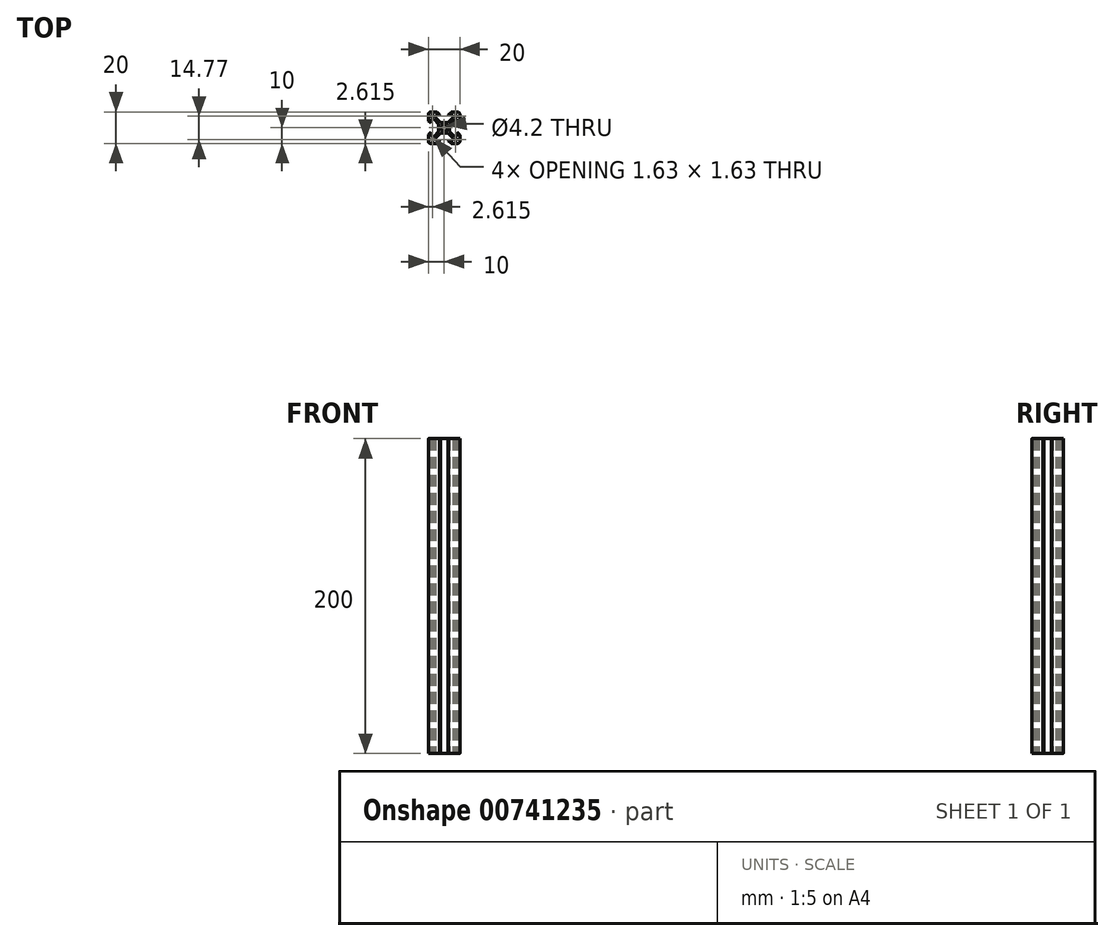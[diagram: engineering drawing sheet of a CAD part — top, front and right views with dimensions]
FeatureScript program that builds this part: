
annotation { "Feature Type Name" : "Feature", "Feature Type Description" : "" }
export const myFeature = defineFeature(function(context is Context, id is Id, definition is map)
    precondition{}
    {
        {
            var Q0;
            Q0=qCreatedBy(makeId("Top.planeOp"),FACE);
            var sketch = newSketch(context, id + "F0", { "sketchPlane" : qUnion([Q0])});
            skLineSegment(sketch, "E0", {"start": v(-8.2, -8.2) * mm, "end": v(-6.57, -8.2) * mm});
            skLineSegment(sketch, "E1", {"start": v(-8.2, -6.57) * mm, "end": v(-8.2, -8.2) * mm});
            skLineSegment(sketch, "E2", {"start": v(-7.66, -6.57) * mm, "end": v(-8.2, -6.57) * mm});
            skLineSegment(sketch, "E3", {"start": v(-6.57, -7.66) * mm, "end": v(-7.66, -6.57) * mm});
            skLineSegment(sketch, "E4", {"start": v(-6.57, -8.2) * mm, "end": v(-6.57, -7.66) * mm});
            skLineSegment(sketch, "E5", {"start": v(7.66, -6.57) * mm, "end": v(6.57, -7.66) * mm});
            skLineSegment(sketch, "E6", {"start": v(8.2, -6.57) * mm, "end": v(7.66, -6.57) * mm});
            skLineSegment(sketch, "E7", {"start": v(8.2, -8.2) * mm, "end": v(8.2, -6.57) * mm});
            skLineSegment(sketch, "E8", {"start": v(6.57, -8.2) * mm, "end": v(8.2, -8.2) * mm});
            skLineSegment(sketch, "E9", {"start": v(6.57, -7.66) * mm, "end": v(6.57, -8.2) * mm});
            skCircle(sketch, "E10", {"center": v(0, 0) * mm, "radius": 2.1 * mm});
            skLineSegment(sketch, "E11", {"start": v(8.2, 8.2) * mm, "end": v(6.57, 8.2) * mm});
            skLineSegment(sketch, "E12", {"start": v(8.2, 6.57) * mm, "end": v(8.2, 8.2) * mm});
            skLineSegment(sketch, "E13", {"start": v(7.66, 6.57) * mm, "end": v(8.2, 6.57) * mm});
            skLineSegment(sketch, "E14", {"start": v(6.57, 7.66) * mm, "end": v(7.66, 6.57) * mm});
            skLineSegment(sketch, "E15", {"start": v(6.57, 8.2) * mm, "end": v(6.57, 7.66) * mm});
            skLineSegment(sketch, "E16", {"start": v(-7.66, 6.57) * mm, "end": v(-6.57, 7.66) * mm});
            skLineSegment(sketch, "E17", {"start": v(-8.2, 6.57) * mm, "end": v(-7.66, 6.57) * mm});
            skLineSegment(sketch, "E18", {"start": v(-8.2, 8.2) * mm, "end": v(-8.2, 6.57) * mm});
            skLineSegment(sketch, "E19", {"start": v(-6.57, 8.2) * mm, "end": v(-8.2, 8.2) * mm});
            skLineSegment(sketch, "E20", {"start": v(-6.57, 7.66) * mm, "end": v(-6.57, 8.2) * mm});
            skLineSegment(sketch, "E21", {"start": v(-6.56, 5.5) * mm, "end": v(-3.4, 2.34) * mm});
            skLineSegment(sketch, "E22", {"start": v(-3.4, 2.34) * mm, "end": v(-3.4, -2.34) * mm});
            skLineSegment(sketch, "E23", {"start": v(-3.4, -2.34) * mm, "end": v(-6.56, -5.5) * mm});
            skLineSegment(sketch, "E24", {"start": v(-6.56, -5.5) * mm, "end": v(-8.2, -5.5) * mm});
            skLineSegment(sketch, "E25", {"start": v(-8.2, -5.5) * mm, "end": v(-8.2, -2.89) * mm});
            skLineSegment(sketch, "E26", {"start": v(-8.2, -2.9) * mm, "end": v(-8.31, -2.9) * mm});
            skLineSegment(sketch, "E27", {"start": v(-8.31, -2.9) * mm, "end": v(-9.77, -4.35) * mm});
            skArc(sketch, "E28", {"start": v(-9.77, -4.35) * mm, "mid": v(-9.94, -4.6) * mm, "end": v(-10, -4.9) * mm});
            skLineSegment(sketch, "E29", {"start": v(-10, -4.9) * mm, "end": v(-10, -8.5) * mm});
            skArc(sketch, "E30", {"start": v(-10, -8.5) * mm, "mid": v(-9.56, -9.56) * mm, "end": v(-8.5, -10) * mm});
            skLineSegment(sketch, "E31", {"start": v(-8.5, -10) * mm, "end": v(-4.9, -10) * mm});
            skArc(sketch, "E32", {"start": v(-4.9, -10) * mm, "mid": v(-4.6, -9.94) * mm, "end": v(-4.35, -9.77) * mm});
            skLineSegment(sketch, "E33", {"start": v(-4.35, -9.77) * mm, "end": v(-2.9, -8.31) * mm});
            skLineSegment(sketch, "E34", {"start": v(-2.89, -8.31) * mm, "end": v(-2.89, -8.2) * mm});
            skLineSegment(sketch, "E35", {"start": v(-2.89, -8.2) * mm, "end": v(-5.5, -8.2) * mm});
            skLineSegment(sketch, "E36", {"start": v(-5.5, -8.2) * mm, "end": v(-5.5, -6.56) * mm});
            skLineSegment(sketch, "E37", {"start": v(-5.5, -6.56) * mm, "end": v(-2.34, -3.4) * mm});
            skLineSegment(sketch, "E38", {"start": v(-2.34, -3.4) * mm, "end": v(2.34, -3.4) * mm});
            skLineSegment(sketch, "E39", {"start": v(2.34, -3.4) * mm, "end": v(5.5, -6.56) * mm});
            skLineSegment(sketch, "E40", {"start": v(5.5, -6.56) * mm, "end": v(5.5, -8.2) * mm});
            skLineSegment(sketch, "E41", {"start": v(5.5, -8.2) * mm, "end": v(2.9, -8.2) * mm});
            skLineSegment(sketch, "E42", {"start": v(2.9, -8.2) * mm, "end": v(2.9, -8.31) * mm});
            skLineSegment(sketch, "E43", {"start": v(2.9, -8.31) * mm, "end": v(4.35, -9.77) * mm});
            skArc(sketch, "E44", {"start": v(4.35, -9.77) * mm, "mid": v(4.6, -9.94) * mm, "end": v(4.9, -10) * mm});
            skLineSegment(sketch, "E45", {"start": v(4.9, -10) * mm, "end": v(8.5, -10) * mm});
            skArc(sketch, "E46", {"start": v(8.5, -10) * mm, "mid": v(9.56, -9.56) * mm, "end": v(10, -8.5) * mm});
            skLineSegment(sketch, "E47", {"start": v(10, -8.5) * mm, "end": v(10, -4.9) * mm});
            skArc(sketch, "E48", {"start": v(10, -4.9) * mm, "mid": v(9.94, -4.6) * mm, "end": v(9.77, -4.35) * mm});
            skLineSegment(sketch, "E49", {"start": v(9.77, -4.35) * mm, "end": v(8.31, -2.89) * mm});
            skLineSegment(sketch, "E50", {"start": v(8.31, -2.9) * mm, "end": v(8.2, -2.9) * mm});
            skLineSegment(sketch, "E51", {"start": v(8.2, -2.9) * mm, "end": v(8.2, -5.5) * mm});
            skLineSegment(sketch, "E52", {"start": v(8.2, -5.5) * mm, "end": v(6.56, -5.5) * mm});
            skLineSegment(sketch, "E53", {"start": v(6.56, -5.5) * mm, "end": v(3.4, -2.34) * mm});
            skLineSegment(sketch, "E54", {"start": v(3.4, -2.34) * mm, "end": v(3.4, 2.34) * mm});
            skLineSegment(sketch, "E55", {"start": v(3.4, 2.34) * mm, "end": v(6.56, 5.5) * mm});
            skLineSegment(sketch, "E56", {"start": v(6.56, 5.5) * mm, "end": v(8.2, 5.5) * mm});
            skLineSegment(sketch, "E57", {"start": v(8.2, 5.5) * mm, "end": v(8.2, 2.9) * mm});
            skLineSegment(sketch, "E58", {"start": v(8.2, 2.9) * mm, "end": v(8.31, 2.9) * mm});
            skLineSegment(sketch, "E59", {"start": v(8.31, 2.9) * mm, "end": v(9.77, 4.35) * mm});
            skArc(sketch, "E60", {"start": v(9.77, 4.35) * mm, "mid": v(9.94, 4.6) * mm, "end": v(10, 4.9) * mm});
            skLineSegment(sketch, "E61", {"start": v(10, 4.9) * mm, "end": v(10, 8.5) * mm});
            skArc(sketch, "E62", {"start": v(10, 8.5) * mm, "mid": v(9.56, 9.56) * mm, "end": v(8.5, 10) * mm});
            skLineSegment(sketch, "E63", {"start": v(8.5, 10) * mm, "end": v(4.9, 10) * mm});
            skArc(sketch, "E64", {"start": v(4.9, 10) * mm, "mid": v(4.6, 9.94) * mm, "end": v(4.35, 9.77) * mm});
            skLineSegment(sketch, "E65", {"start": v(4.35, 9.77) * mm, "end": v(2.9, 8.31) * mm});
            skLineSegment(sketch, "E66", {"start": v(2.9, 8.31) * mm, "end": v(2.9, 8.2) * mm});
            skLineSegment(sketch, "E67", {"start": v(2.9, 8.2) * mm, "end": v(5.5, 8.2) * mm});
            skLineSegment(sketch, "E68", {"start": v(5.5, 8.2) * mm, "end": v(5.5, 6.56) * mm});
            skLineSegment(sketch, "E69", {"start": v(5.5, 6.56) * mm, "end": v(2.34, 3.4) * mm});
            skLineSegment(sketch, "E70", {"start": v(2.34, 3.4) * mm, "end": v(-2.34, 3.4) * mm});
            skLineSegment(sketch, "E71", {"start": v(-2.34, 3.4) * mm, "end": v(-5.5, 6.56) * mm});
            skLineSegment(sketch, "E72", {"start": v(-5.5, 6.56) * mm, "end": v(-5.5, 8.2) * mm});
            skLineSegment(sketch, "E73", {"start": v(-5.5, 8.2) * mm, "end": v(-2.9, 8.2) * mm});
            skLineSegment(sketch, "E74", {"start": v(-2.89, 8.2) * mm, "end": v(-2.89, 8.31) * mm});
            skLineSegment(sketch, "E75", {"start": v(-2.89, 8.31) * mm, "end": v(-4.35, 9.77) * mm});
            skArc(sketch, "E76", {"start": v(-4.35, 9.77) * mm, "mid": v(-4.6, 9.94) * mm, "end": v(-4.9, 10) * mm});
            skLineSegment(sketch, "E77", {"start": v(-4.9, 10) * mm, "end": v(-8.5, 10) * mm});
            skArc(sketch, "E78", {"start": v(-8.5, 10) * mm, "mid": v(-9.56, 9.56) * mm, "end": v(-10, 8.5) * mm});
            skLineSegment(sketch, "E79", {"start": v(-10, 8.5) * mm, "end": v(-10, 4.9) * mm});
            skArc(sketch, "E80", {"start": v(-10, 4.9) * mm, "mid": v(-9.94, 4.6) * mm, "end": v(-9.77, 4.35) * mm});
            skLineSegment(sketch, "E81", {"start": v(-9.77, 4.35) * mm, "end": v(-8.31, 2.9) * mm});
            skLineSegment(sketch, "E82", {"start": v(-8.31, 2.9) * mm, "end": v(-8.2, 2.9) * mm});
            skLineSegment(sketch, "E83", {"start": v(-8.2, 2.9) * mm, "end": v(-8.2, 5.5) * mm});
            skLineSegment(sketch, "E84", {"start": v(-8.2, 5.5) * mm, "end": v(-6.56, 5.5) * mm});
            skSolve(sketch);
        }
        {
            var Q0;
            Q0 = qSketchRegion(id + "F0", true);
            extrude(context, id + "F1", {"entities" : qUnion([Q0]), "depth" : 200 * mm, "offsetDistance" : 25 * mm});
        }
    });
